# Revit family: LC 140 types Sans hôte
name_source: partatom
category: Dispositifs d'éclairage
units: mm (PartAtom-declared; Revit-internal decimal feet)

## family parameters
Basée sur le plan de construction = Non
Conserver l'orientation des annotations = Non
Cote de connecteur circulaire = Utiliser le diamètre
Couper avec des vides une fois chargée = Non
Partagée = Non
Point de calcul de pièce = Non
Toujours verticalement = Oui
Type d'élément = Normal

## types (3) — shared parameters
Alimentation = 110-240 V AC
Classe = II
Code d'assemblage = D5010200
Elévation par défaut = 250 cm
Fabricant = B.E.G.
Hauteur de montage max = 400 cm
Image du type = MURAL.JPG
Marque = LUXOMAT
Mode de pose = Mural
Position en hauteur = 250 cm
Température ambiante = -25°C à + 50°C
URL = http://www.luxomat.com

## per-type parameters (varying)
| type | Charge Cos ɸ =0.5 | Charge Cos ɸ =1 | Charge LED | Commentaires du type | Consommation | IP | Modèle | Relais | Référence | Type de Sortie |
| 01- LC 140 Générique |  |  |  | DET.MOUV.140°/12M MURAL |  | 54 | LC 140 |  |  |  |
| 02- LC N 140 réf 91001 | 500 VA | 1000 W | 200 W | DET.MOUV.1 CONTACT.140°/12M MURAL | 0.4 W | 54 | LC N 140 | 4.3 A | 91001 | TOR |
| 03- LC 140 réf 91101 | 500 VA | 1000 W | 0 | DET.MOUV.1 CONTACT.140°/12M MURAL SANS DETECTION VERTICALE | 0.4 W | 44 | LC 140 | 4.3 A | 91101 | TOR |
